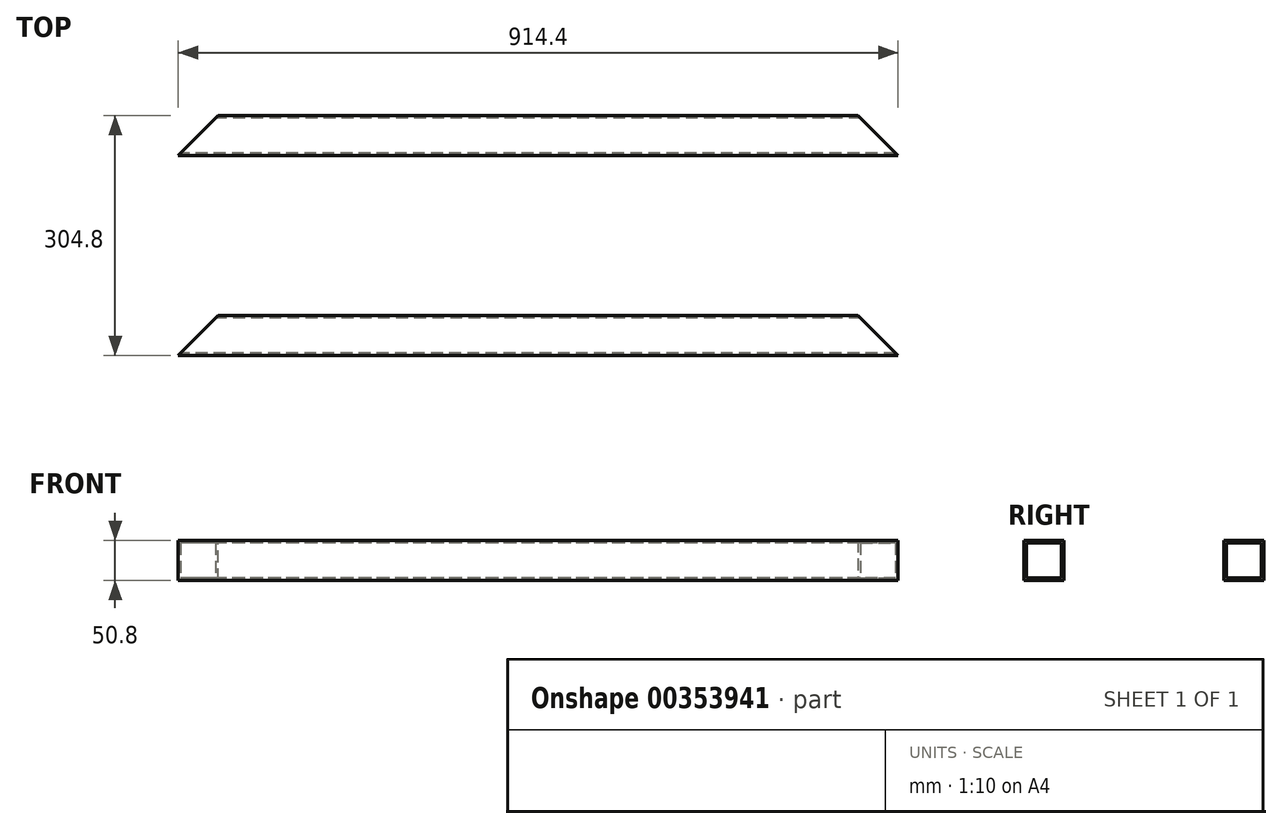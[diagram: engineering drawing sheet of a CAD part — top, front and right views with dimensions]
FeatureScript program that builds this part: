
annotation { "Feature Type Name" : "Feature", "Feature Type Description" : "" }
export const myFeature = defineFeature(function(context is Context, id is Id, definition is map)
    precondition{}
    {
        {
            var Q0;
            Q0=qCreatedBy(makeId("Front.planeOp"),FACE);
            var sketch = newSketch(context, id + "F0", { "sketchPlane" : qUnion([Q0])});
            skLineSegment(sketch, "E0.bottom", {"start": v(457.2, 25.4) * mm, "end": v(-457.2, 25.4) * mm});
            skLineSegment(sketch, "E0.top", {"start": v(457.2, -25.4) * mm, "end": v(-457.2, -25.4) * mm});
            skLineSegment(sketch, "E0.left", {"start": v(457.2, 25.4) * mm, "end": v(457.2, -25.4) * mm});
            skLineSegment(sketch, "E0.right", {"start": v(-457.2, 25.4) * mm, "end": v(-457.2, -25.4) * mm});
            skPoint(sketch, "E0.middle", {"position": v(0, 0) * mm});
            skSolve(sketch);
        }
        {
            var Q0;
            Q0 = qSketchRegion(id + "F0", true);
            extrude(context, id + "F1", {"entities" : qUnion([Q0]), "depth" : 50.8 * mm});
        }
        {
            var Q0;
            Q0=makeQuery(id+"F1.opExtrude","SWEPT_FACE",FACE,{"disambiguationData":[OSD([sQuery(id+"F0.wireOp",EDGE,"E0.right")])]});
            var sketch = newSketch(context, id + "F2", { "sketchPlane" : qUnion([Q0])});
            skLineSegment(sketch, "E1.bottom", {"start": v(47.63, -22.23) * mm, "end": v(3.18, -22.23) * mm});
            skLineSegment(sketch, "E1.top", {"start": v(47.63, 22.23) * mm, "end": v(3.18, 22.23) * mm});
            skLineSegment(sketch, "E1.left", {"start": v(47.63, -22.23) * mm, "end": v(47.63, 22.23) * mm});
            skLineSegment(sketch, "E1.right", {"start": v(3.18, -22.23) * mm, "end": v(3.17, 22.23) * mm});
            skPoint(sketch, "E1.middle", {"position": v(25.4, 0) * mm});
            skSolve(sketch);
        }
        {
            var Q0;
            Q0 = qSketchRegion(id + "F2", true);
            extrude(context, id + "F3", {"entities" : qUnion([Q0]), "operationType" : NewBodyOperationType.REMOVE, "endBound" : BoundingType.THROUGH_ALL, "oppositeDirection" : true, "depth" : 25.4 * mm});
        }
        {
            var Q0;
            Q0=makeQuery(id+"F1.opExtrude","CAP_EDGE",EDGE,{"disambiguationData":[OSD([sQuery(id+"F0.wireOp",EDGE,"E0.left")])],"isStart":true});
            var Q1;
            Q1=makeQuery(id+"F1.opExtrude","CAP_EDGE",EDGE,{"disambiguationData":[OSD([sQuery(id+"F0.wireOp",EDGE,"E0.right")])],"isStart":true});
            chamfer(context, id + "F4", {"entities" : qUnion([Q0, Q1]), "width" : 50.8 * mm, "tangentPropagation" : true});
        }
        {
            var Q0;
            Q0=makeQuery(id+"F1.opExtrude","SWEPT_BODY",BODY,{"disambiguationData":[OSD([sQuery(id+"F0.wireOp",EDGE,"E0.bottom"),sQuery(id+"F0.wireOp",EDGE,"E0.top"),sQuery(id+"F0.wireOp",EDGE,"E0.left"),sQuery(id+"F0.wireOp",EDGE,"E0.right")])]});
            transform(context, id + "F5", {"entities" : qUnion([Q0]), "transformType" : TransformType.TRANSLATION_3D, "dx" : 0 * mm, "dy" : 254 * mm, "dz" : 0 * mm, "makeCopy" : true});
        }
    });
